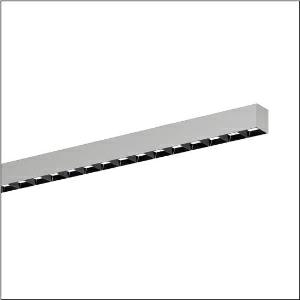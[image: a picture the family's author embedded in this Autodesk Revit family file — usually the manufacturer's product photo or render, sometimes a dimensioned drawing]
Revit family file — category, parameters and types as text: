
# Revit family: silica_r__21_51mx24tat4s_af2d
name_source: partatom
category: Lighting Fixtures
units: mm (PartAtom-declared; Revit-internal decimal feet)

## family parameters
Cut with Voids When Loaded = No
Host = Face
Light Source = No
Part Type = Normal
Room Calculation Point = No
Round Connector Dimension = Use Diameter
Shared = No

## types (1)
- --- (1 x LED, 3280 lm, 32.4 W, 6500K)
    Apparent Load = 32 VA
    CIE Flux Codes = 74 94 99 100 100
    Color Rendering = 80
    Color Temperature = 6500K
    Default Elevation = 1800 mm
    Description = Silica® 21, office luminaire, primary light control with darklight reflector, of PMMA, black, light emission: direct distribution, primary light characteristic: asymmetric, installation type: surface-mounted, LED, rated luminous flux: 3.280lm, luminous efficacy: 96lm/W, light colour: 8tw, colour temperature: 2700..6500K, control gear: ECG DALI, with terminal, 3+2-pole, max. 2.5mm², mains connection: 220..240V, AC, 50/60Hz, rated input power: 34.1W, luminaire housing, of aluminium, metallic grey (RAL 9006), length: 1.204mm, width: 53mm, height: 53mm, protection rating (complete): IP20, insulation class (complete): insulation class I (protective earthing), certification: CE, permissible operating ambient temperature: 0..+35°C, standard: EN 50419, packaging unit: 1 piece
    Height = 0 mm  [stored 0 ft]
    Lamp = 1 x LED
    Lamp Light Flux = 3280 lm
    Lamp Power = 32.4 W
    Lamp count = 1
    Length = 1204 mm
    Luminous efficacy = 101 lm/W
    Manufacturer = Siteco
    ModVariant = No
    Model = 51MX24TAT4S
    Mounting Place = Ceiling
    Mounting Type = Recessed
    Number of Poles = 1
    OnlyDefault = Yes
    Power Factor = 1
    Product Name = Silica® 21
    Product group = office luminaire | ceiling recessed
    ProductGroupID = 401
    Protection Class = Protection class I
    Protection Degree = IP 20
    RLX_Detail_Level = 1
    RLX_Emergency_Light_Flux = 0 lm
    RLX_Emergency_Type = 0
    RLX_Emergency_Type_DB = No
    RlxData = <blob elided: 39853 chars, md5=063a2f0c>
    Socket = socket
    Standby Power = 0 W
    System Light Flux = 3280 lm
    System Power = 32 W
    Type Comments = individual setting
    Type Image = l_1313585.jpg
    URL = http://relux.com
    VarID = @adj_089349
    Voltage = 0 V
    Weight = 0.00 kg
    Width = 53 mm

note: [stored X ft] marks values corroborated as IEEE doubles in the binary element streams (Revit-internal decimal feet)

## geometry (parser evidence)
native form markers: Blend x4, Sweep x10
no freeform markers — native parametric forms only
